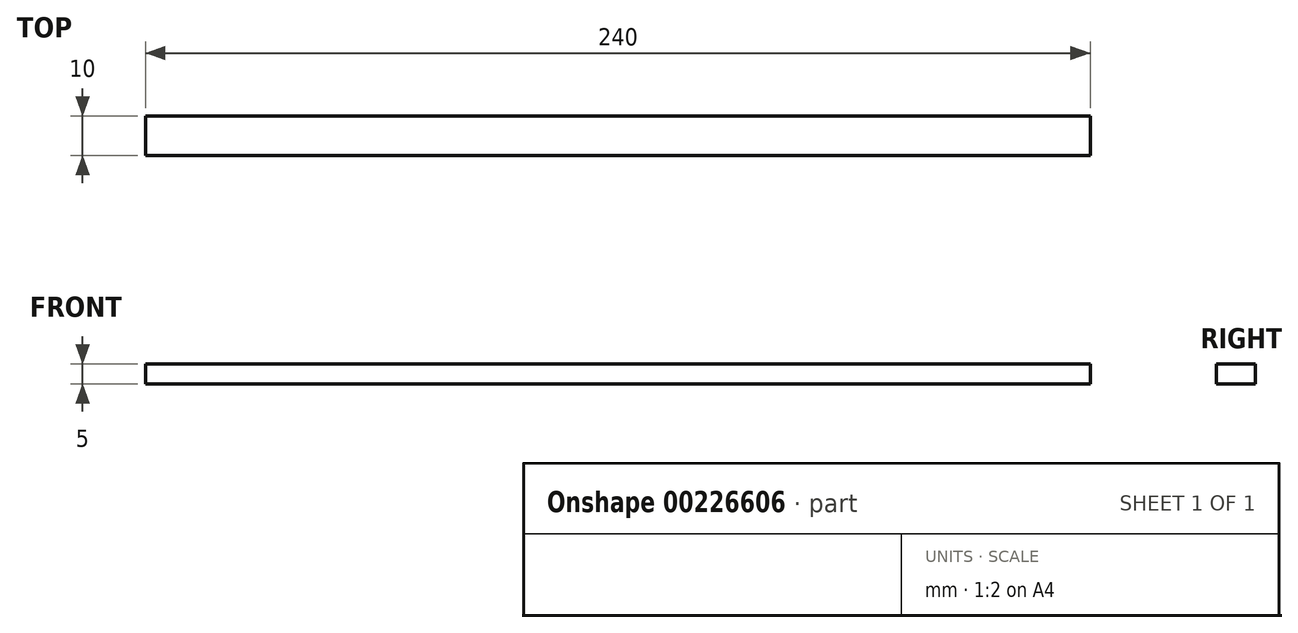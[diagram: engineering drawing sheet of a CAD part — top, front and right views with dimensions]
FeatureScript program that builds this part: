
annotation { "Feature Type Name" : "Feature", "Feature Type Description" : "" }
export const myFeature = defineFeature(function(context is Context, id is Id, definition is map)
    precondition{}
    {
        {
            var Q0;
            Q0=qCreatedBy(makeId("Top.planeOp"),FACE);
            var sketch = newSketch(context, id + "F0", { "sketchPlane" : qUnion([Q0])});
            skLineSegment(sketch, "E0.bottom", {"start": v(-120, 5) * mm, "end": v(120, 5) * mm});
            skLineSegment(sketch, "E0.top", {"start": v(-120, -5) * mm, "end": v(120, -5) * mm});
            skLineSegment(sketch, "E0.left", {"start": v(-120, 5) * mm, "end": v(-120, -5) * mm});
            skLineSegment(sketch, "E0.right", {"start": v(120, 5) * mm, "end": v(120, -5) * mm});
            skLineSegment(sketch, "E1", {"start": v(-120, -5) * mm, "end": v(120, 5) * mm, "construction": true});
            skLineSegment(sketch, "E2", {"start": v(-120, 5) * mm, "end": v(120, -5) * mm, "construction": true});
            skSolve(sketch);
        }
        {
            var Q0;
            Q0 = qSketchRegion(id + "F0", true);
            extrude(context, id + "F1", {"entities" : qUnion([Q0]), "depth" : 5 * mm});
        }
    });
